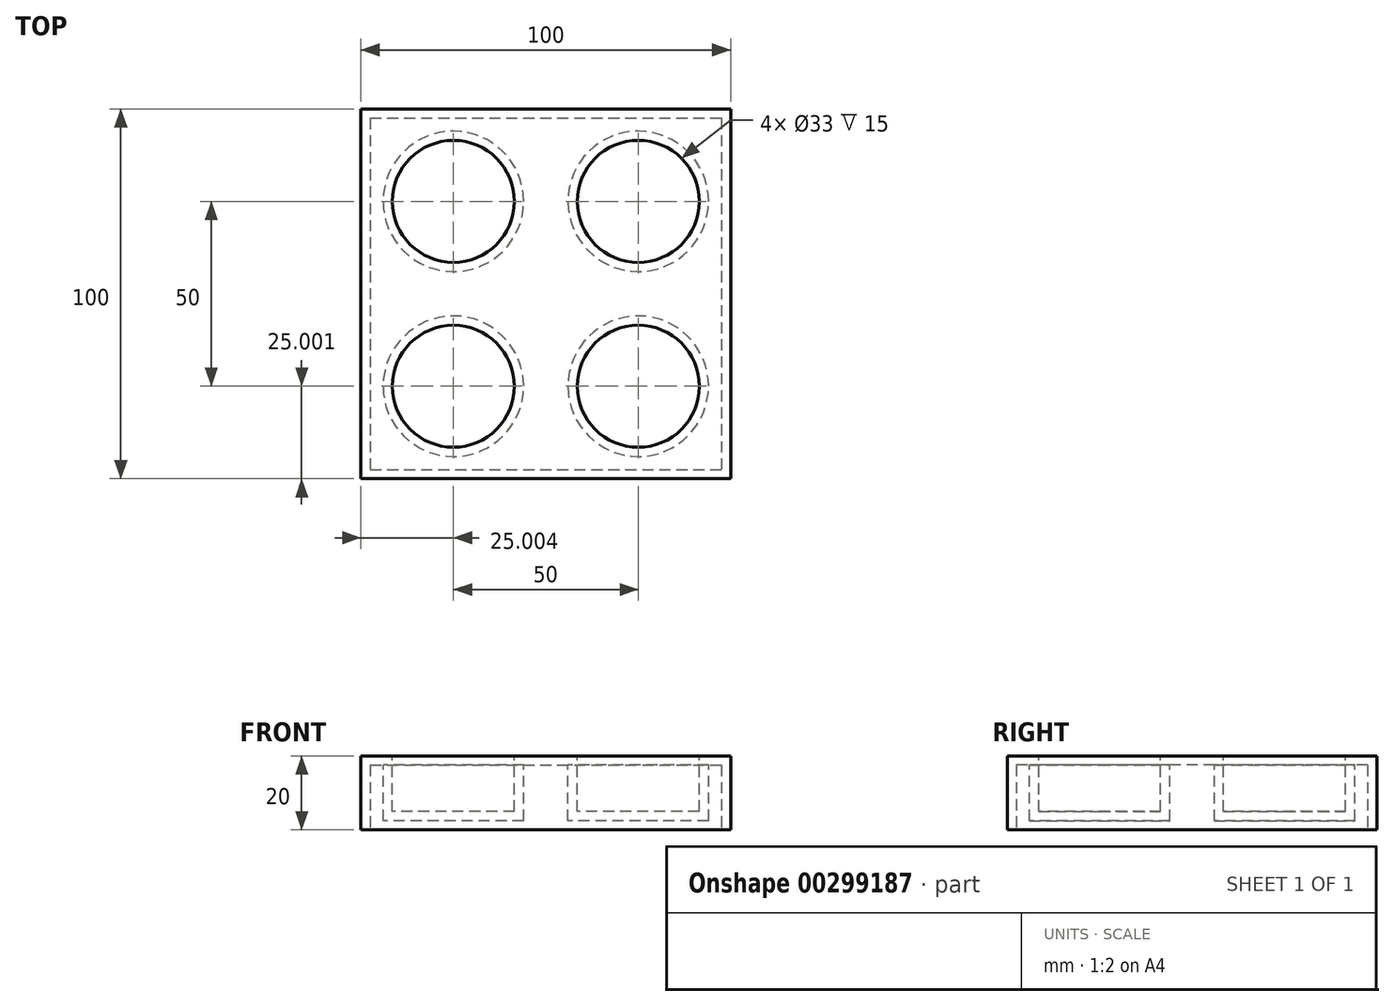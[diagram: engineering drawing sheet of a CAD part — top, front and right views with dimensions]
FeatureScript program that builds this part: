
annotation { "Feature Type Name" : "Feature", "Feature Type Description" : "" }
export const myFeature = defineFeature(function(context is Context, id is Id, definition is map)
    precondition{}
    {
        {
            var Q0;
            Q0=qCreatedBy(makeId("Top.planeOp"),FACE);
            var sketch = newSketch(context, id + "F0", { "sketchPlane" : qUnion([Q0])});
            skLineSegment(sketch, "E0.bottom", {"start": v(-23.02, 69.66) * mm, "end": v(76.98, 69.66) * mm});
            skLineSegment(sketch, "E0.top", {"start": v(-23.02, -30.34) * mm, "end": v(76.98, -30.34) * mm});
            skLineSegment(sketch, "E0.left", {"start": v(-23.02, 69.66) * mm, "end": v(-23.02, -30.34) * mm});
            skLineSegment(sketch, "E0.right", {"start": v(76.98, 69.66) * mm, "end": v(76.98, -30.34) * mm});
            skSolve(sketch);
        }
        {
            var Q0;
            Q0=makeQuery(id+"F0.imprint","IMPRINT",FACE,{"disambiguationData":[TD([[makeQuery(id+"F0.imprint","IMPRINT",EDGE,{"derivedFrom":sQuery(id+"F0.wireOp",EDGE,"E0.bottom")}),-1.0]])]});
            extrude(context, id + "F1", {"entities" : qUnion([Q0]), "depth" : 20 * mm});
        }
        {
            var Q0;
            Q0=makeQuery(id+"F1.opExtrude","CAP_FACE",FACE,{"disambiguationData":[OSD([sQuery(id+"F0.wireOp",EDGE,"E0.bottom"),sQuery(id+"F0.wireOp",EDGE,"E0.top"),sQuery(id+"F0.wireOp",EDGE,"E0.left"),sQuery(id+"F0.wireOp",EDGE,"E0.right")])],"isStart":false});
            var sketch = newSketch(context, id + "F2", { "sketchPlane" : qUnion([Q0])});
            skLineSegment(sketch, "E1", {"start": v(26.98, 69.66) * mm, "end": v(26.98, -30.34) * mm});
            skLineSegment(sketch, "E2", {"start": v(-23.02, 19.66) * mm, "end": v(76.98, 19.66) * mm});
            skLineSegment(sketch, "E3", {"start": v(76.98, 19.66) * mm, "end": v(77.82, 18.03) * mm});
            skCircle(sketch, "E4", {"center": v(1.98, 44.66) * mm, "radius": 16.5 * mm});
            skCircle(sketch, "E5", {"center": v(51.98, 44.66) * mm, "radius": 16.5 * mm});
            skCircle(sketch, "E6", {"center": v(51.98, -5.34) * mm, "radius": 16.5 * mm});
            skCircle(sketch, "E7", {"center": v(1.98, -5.34) * mm, "radius": 16.5 * mm});
            skSolve(sketch);
        }
        {
            var Q0;
            Q0=makeQuery(id+"F2.imprint","IMPRINT",FACE,{"disambiguationData":[TD([[makeQuery(id+"F2.imprint","IMPRINT",EDGE,{"derivedFrom":sQuery(id+"F2.wireOp",EDGE,"E4")}),1.0]])]});
            var Q1;
            Q1=makeQuery(id+"F2.imprint","IMPRINT",FACE,{"disambiguationData":[TD([[makeQuery(id+"F2.imprint","IMPRINT",EDGE,{"derivedFrom":sQuery(id+"F2.wireOp",EDGE,"E5")}),1.0]])]});
            var Q2;
            Q2=makeQuery(id+"F2.imprint","IMPRINT",FACE,{"disambiguationData":[TD([[makeQuery(id+"F2.imprint","IMPRINT",EDGE,{"derivedFrom":sQuery(id+"F2.wireOp",EDGE,"E6")}),1.0]])]});
            var Q3;
            Q3=makeQuery(id+"F2.imprint","IMPRINT",FACE,{"disambiguationData":[TD([[makeQuery(id+"F2.imprint","IMPRINT",EDGE,{"derivedFrom":sQuery(id+"F2.wireOp",EDGE,"E7")}),1.0]])]});
            extrude(context, id + "F3", {"entities" : qUnion([Q0, Q1, Q2, Q3]), "operationType" : NewBodyOperationType.REMOVE, "oppositeDirection" : true, "depth" : 15 * mm});
        }
        {
            var Q0;
            Q0=makeQuery(id+"F1.opExtrude","CAP_FACE",FACE,{"disambiguationData":[OSD([sQuery(id+"F0.wireOp",EDGE,"E0.bottom"),sQuery(id+"F0.wireOp",EDGE,"E0.top"),sQuery(id+"F0.wireOp",EDGE,"E0.left"),sQuery(id+"F0.wireOp",EDGE,"E0.right")])],"isStart":true});
            shell(context, id + "F4", {"entities" : qUnion([Q0]), "thickness" : 2.5 * mm});
        }
    });
